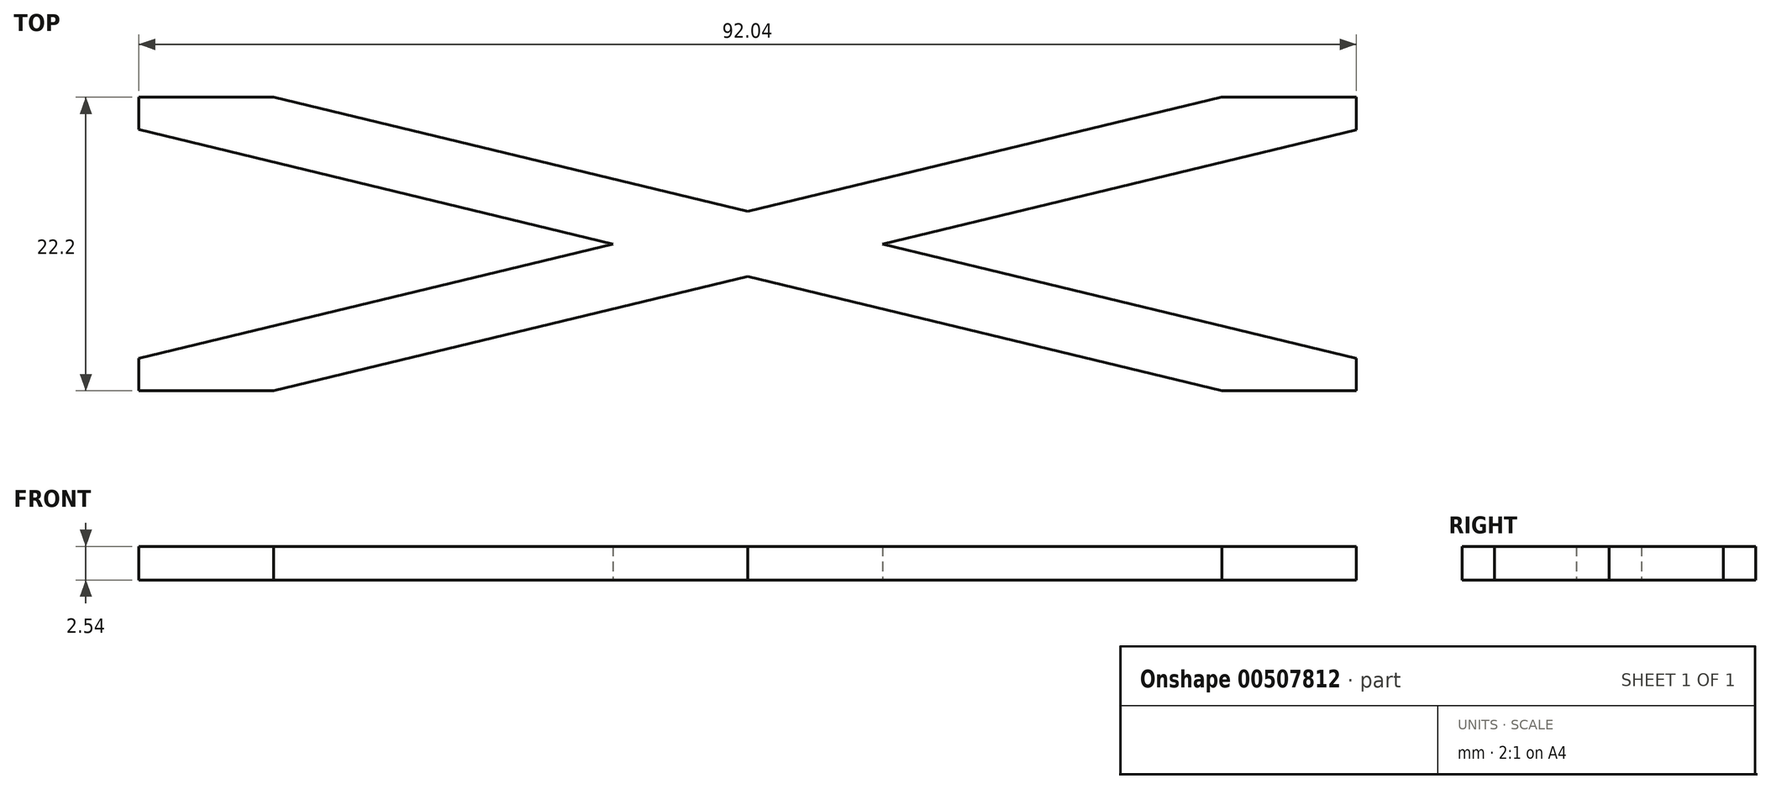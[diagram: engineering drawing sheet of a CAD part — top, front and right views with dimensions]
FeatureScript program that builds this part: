
annotation { "Feature Type Name" : "Feature", "Feature Type Description" : "" }
export const myFeature = defineFeature(function(context is Context, id is Id, definition is map)
    precondition{}
    {
        {
            var Q0;
            Q0=qCreatedBy(makeId("Top.planeOp"),FACE);
            var sketch = newSketch(context, id + "F0", { "sketchPlane" : qUnion([Q0])});
            skLineSegment(sketch, "E0.bottom", {"start": v(-46.02, 11.1) * mm, "end": v(46.02, 11.1) * mm, "construction": true});
            skLineSegment(sketch, "E0.top", {"start": v(-46.02, -11.1) * mm, "end": v(46.02, -11.1) * mm, "construction": true});
            skLineSegment(sketch, "E0.left", {"start": v(-46.02, 11.1) * mm, "end": v(-46.02, -11.1) * mm, "construction": true});
            skLineSegment(sketch, "E0.right", {"start": v(46.02, 11.1) * mm, "end": v(46.02, -11.1) * mm, "construction": true});
            skLineSegment(sketch, "E1", {"start": v(-46.02, -11.1) * mm, "end": v(46.02, 11.1) * mm, "construction": true});
            skLineSegment(sketch, "E2", {"start": v(-46.02, 11.1) * mm, "end": v(46.02, -11.1) * mm, "construction": true});
            skLineSegment(sketch, "E3", {"start": v(-46.02, 8.65) * mm, "end": v(-10.17, 0) * mm});
            skLineSegment(sketch, "E4", {"start": v(-35.81, 11.1) * mm, "end": v(0.01, 2.46) * mm});
            skLineSegment(sketch, "E5", {"start": v(-46.02, 11.1) * mm, "end": v(-46.02, 8.65) * mm});
            skLineSegment(sketch, "E6", {"start": v(-46.02, 8.65) * mm, "end": v(-46.02, 11.1) * mm});
            skLineSegment(sketch, "E7", {"start": v(-46.02, 11.1) * mm, "end": v(-35.81, 11.1) * mm});
            skLineSegment(sketch, "E8", {"start": v(-46.02, -8.64) * mm, "end": v(-10.17, 0) * mm});
            skLineSegment(sketch, "E9", {"start": v(-35.84, -11.1) * mm, "end": v(0.01, -2.45) * mm});
            skLineSegment(sketch, "E10", {"start": v(-46.02, -11.1) * mm, "end": v(-46.02, -8.64) * mm});
            skLineSegment(sketch, "E11", {"start": v(-46.02, -8.64) * mm, "end": v(-46.02, -11.1) * mm});
            skLineSegment(sketch, "E12", {"start": v(-46.02, -11.1) * mm, "end": v(-35.84, -11.1) * mm});
            skLineSegment(sketch, "E13", {"start": v(35.84, 11.1) * mm, "end": v(46.02, 11.1) * mm});
            skLineSegment(sketch, "E14", {"start": v(46.02, 11.1) * mm, "end": v(46.02, 8.64) * mm});
            skLineSegment(sketch, "E15", {"start": v(46.02, -8.64) * mm, "end": v(46.02, -11.1) * mm});
            skLineSegment(sketch, "E16", {"start": v(46.02, -11.1) * mm, "end": v(35.87, -11.1) * mm});
            skLineSegment(sketch, "E17.trimOffspring", {"start": v(0.01, -2.45) * mm, "end": v(35.87, -11.1) * mm});
            skLineSegment(sketch, "E18.trimOffspring", {"start": v(0.01, 2.46) * mm, "end": v(35.84, 11.1) * mm});
            skLineSegment(sketch, "E19.trimOffspring", {"start": v(10.2, 0) * mm, "end": v(46.02, -8.64) * mm});
            skLineSegment(sketch, "E20.trimOffspring", {"start": v(10.2, 0) * mm, "end": v(46.02, 8.64) * mm});
            skSolve(sketch);
        }
        {
            var Q0;
            Q0=makeQuery(id+"F0.imprint","IMPRINT",FACE,{"disambiguationData":[TD([[makeQuery(id+"F0.imprint","IMPRINT",EDGE,{"derivedFrom":sQuery(id+"F0.wireOp",EDGE,"E3")}),1.0]])]});
            extrude(context, id + "F1", {"entities" : qUnion([Q0]), "depth" : 2.54 * mm, "offsetDistance" : 25.4 * mm});
        }
    });
